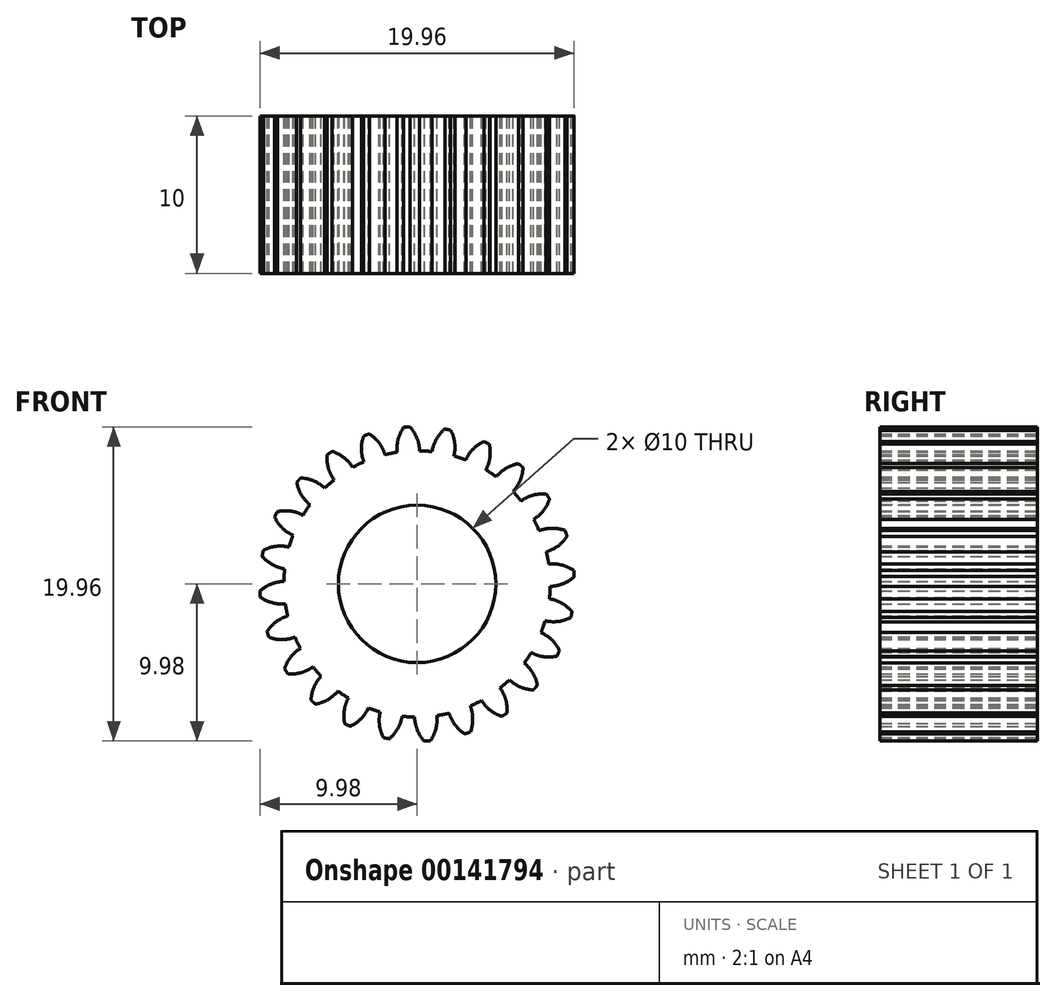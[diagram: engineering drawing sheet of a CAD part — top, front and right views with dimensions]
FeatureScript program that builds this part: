
annotation { "Feature Type Name" : "Feature", "Feature Type Description" : "" }
export const myFeature = defineFeature(function(context is Context, id is Id, definition is map)
    precondition{}
    {
        {
            var Q0;
            Q0=qCreatedBy(makeId("Front.planeOp"),FACE);
            var sketch = newSketch(context, id + "F0", { "sketchPlane" : qUnion([Q0])});
            skCircle(sketch, "E0", {"center": v(0, 0) * mm, "radius": 10 * mm, "construction": true});
            skCircle(sketch, "E1", {"center": v(0, 0) * mm, "radius": 8.46 * mm});
            skCircle(sketch, "E2", {"center": v(0, 0) * mm, "radius": 9.24 * mm, "construction": true});
            skLineSegment(sketch, "E3", {"start": v(0, 0) * mm, "end": v(0, 13.37) * mm, "construction": true});
            skLineSegment(sketch, "E4", {"start": v(0, 0) * mm, "end": v(-0.84, 12.82) * mm, "construction": true});
            skCircle(sketch, "E5", {"center": v(0, 9.24) * mm, "radius": 2.3 * mm, "construction": true});
            skLineSegment(sketch, "E6", {"start": v(0, 9.24) * mm, "end": v(-7.1, 9.24) * mm, "construction": true});
            skLineSegment(sketch, "E7", {"start": v(0, 9.24) * mm, "end": v(-6.72, 6.8) * mm, "construction": true});
            skCircle(sketch, "E8", {"center": v(0, 0) * mm, "radius": 8.68 * mm, "construction": true});
            skArc(sketch, "E9", {"start": v(0, 9.24) * mm, "mid": v(-0.2, 9.63) * mm, "end": v(-0.46, 9.98) * mm});
            skArc(sketch, "E10", {"start": v(0.15, 8.46) * mm, "mid": v(0.11, 8.86) * mm, "end": v(0, 9.24) * mm});
            skArc(sketch, "E11.MirrorCS", {"start": v(-1.2, 9.16) * mm, "mid": v(-1.06, 9.58) * mm, "end": v(-0.85, 9.96) * mm});
            skArc(sketch, "E12.MirrorCS", {"start": v(-1.26, 8.37) * mm, "mid": v(-1.27, 8.77) * mm, "end": v(-1.2, 9.16) * mm});
            skArc(sketch, "E13", {"start": v(-0.46, 9.98) * mm, "mid": v(-0.65, 9.98) * mm, "end": v(-0.85, 9.96) * mm});
            skArc(sketch, "E14.1.0", {"start": v(-3.54, 8.54) * mm, "mid": v(-3.5, 8.97) * mm, "end": v(-3.4, 9.4) * mm});
            skArc(sketch, "E14.1.1", {"start": v(-2.4, 8.93) * mm, "mid": v(-2.68, 9.25) * mm, "end": v(-3.03, 9.52) * mm});
            skArc(sketch, "E14.1.2", {"start": v(-2.04, 8.21) * mm, "mid": v(-2.18, 8.58) * mm, "end": v(-2.4, 8.93) * mm});
            skArc(sketch, "E14.1.3", {"start": v(-3.38, 7.76) * mm, "mid": v(-3.5, 8.14) * mm, "end": v(-3.54, 8.54) * mm});
            skArc(sketch, "E14.1.4", {"start": v(-3.03, 9.52) * mm, "mid": v(-3.21, 9.47) * mm, "end": v(-3.4, 9.4) * mm});
            skArc(sketch, "E14.2.0", {"start": v(-5.62, 7.33) * mm, "mid": v(-5.7, 7.76) * mm, "end": v(-5.71, 8.2) * mm});
            skArc(sketch, "E14.2.1", {"start": v(-4.62, 8) * mm, "mid": v(-4.99, 8.24) * mm, "end": v(-5.39, 8.41) * mm});
            skArc(sketch, "E14.2.2", {"start": v(-4.1, 7.4) * mm, "mid": v(-4.33, 7.73) * mm, "end": v(-4.62, 8) * mm});
            skArc(sketch, "E14.2.3", {"start": v(-5.27, 6.62) * mm, "mid": v(-5.48, 6.96) * mm, "end": v(-5.62, 7.33) * mm});
            skArc(sketch, "E14.2.4", {"start": v(-5.39, 8.41) * mm, "mid": v(-5.55, 8.31) * mm, "end": v(-5.71, 8.2) * mm});
            skArc(sketch, "E14.3.0", {"start": v(-7.33, 5.62) * mm, "mid": v(-7.52, 6.02) * mm, "end": v(-7.64, 6.44) * mm});
            skArc(sketch, "E14.3.1", {"start": v(-6.53, 6.53) * mm, "mid": v(-6.95, 6.67) * mm, "end": v(-7.38, 6.73) * mm});
            skArc(sketch, "E14.3.2", {"start": v(-5.87, 6.1) * mm, "mid": v(-6.18, 6.34) * mm, "end": v(-6.53, 6.53) * mm});
            skArc(sketch, "E14.3.3", {"start": v(-6.8, 5.03) * mm, "mid": v(-7.1, 5.3) * mm, "end": v(-7.33, 5.62) * mm});
            skArc(sketch, "E14.3.4", {"start": v(-7.38, 6.73) * mm, "mid": v(-7.52, 6.6) * mm, "end": v(-7.64, 6.44) * mm});
            skArc(sketch, "E14.4.0", {"start": v(-8.54, 3.54) * mm, "mid": v(-8.82, 3.87) * mm, "end": v(-9.04, 4.25) * mm});
            skArc(sketch, "E14.4.1", {"start": v(-8, 4.62) * mm, "mid": v(-8.44, 4.65) * mm, "end": v(-8.87, 4.6) * mm});
            skArc(sketch, "E14.4.2", {"start": v(-7.25, 4.36) * mm, "mid": v(-7.61, 4.52) * mm, "end": v(-8, 4.62) * mm});
            skArc(sketch, "E14.4.3", {"start": v(-7.87, 3.1) * mm, "mid": v(-8.22, 3.29) * mm, "end": v(-8.54, 3.54) * mm});
            skArc(sketch, "E14.4.4", {"start": v(-8.87, 4.6) * mm, "mid": v(-8.97, 4.42) * mm, "end": v(-9.04, 4.25) * mm});
            skArc(sketch, "E14.5.0", {"start": v(-9.16, 1.2) * mm, "mid": v(-9.52, 1.45) * mm, "end": v(-9.84, 1.76) * mm});
            skArc(sketch, "E14.5.1", {"start": v(-8.93, 2.4) * mm, "mid": v(-9.35, 2.3) * mm, "end": v(-9.76, 2.14) * mm});
            skArc(sketch, "E14.5.2", {"start": v(-8.13, 2.34) * mm, "mid": v(-8.53, 2.4) * mm, "end": v(-8.93, 2.4) * mm});
            skArc(sketch, "E14.5.3", {"start": v(-8.4, 0.95) * mm, "mid": v(-8.8, 1.05) * mm, "end": v(-9.16, 1.2) * mm});
            skArc(sketch, "E14.5.4", {"start": v(-9.76, 2.14) * mm, "mid": v(-9.8, 1.95) * mm, "end": v(-9.84, 1.76) * mm});
            skArc(sketch, "E14.6.0", {"start": v(-9.16, -1.2) * mm, "mid": v(-9.58, -1.06) * mm, "end": v(-9.96, -0.85) * mm});
            skArc(sketch, "E14.6.1", {"start": v(-9.24, 0) * mm, "mid": v(-9.63, -0.2) * mm, "end": v(-9.98, -0.46) * mm});
            skArc(sketch, "E14.6.2", {"start": v(-8.46, 0.15) * mm, "mid": v(-8.86, 0.11) * mm, "end": v(-9.24, 0) * mm});
            skArc(sketch, "E14.6.3", {"start": v(-8.37, -1.26) * mm, "mid": v(-8.77, -1.27) * mm, "end": v(-9.16, -1.2) * mm});
            skArc(sketch, "E14.6.4", {"start": v(-9.98, -0.46) * mm, "mid": v(-9.98, -0.65) * mm, "end": v(-9.96, -0.85) * mm});
            skArc(sketch, "E14.7.0", {"start": v(-8.54, -3.54) * mm, "mid": v(-8.97, -3.5) * mm, "end": v(-9.4, -3.4) * mm});
            skArc(sketch, "E14.7.1", {"start": v(-8.93, -2.4) * mm, "mid": v(-9.25, -2.68) * mm, "end": v(-9.52, -3.03) * mm});
            skArc(sketch, "E14.7.2", {"start": v(-8.21, -2.04) * mm, "mid": v(-8.58, -2.18) * mm, "end": v(-8.93, -2.4) * mm});
            skArc(sketch, "E14.7.3", {"start": v(-7.76, -3.38) * mm, "mid": v(-8.14, -3.5) * mm, "end": v(-8.54, -3.54) * mm});
            skArc(sketch, "E14.7.4", {"start": v(-9.52, -3.03) * mm, "mid": v(-9.47, -3.21) * mm, "end": v(-9.4, -3.4) * mm});
            skArc(sketch, "E14.8.0", {"start": v(-7.33, -5.62) * mm, "mid": v(-7.76, -5.7) * mm, "end": v(-8.2, -5.71) * mm});
            skArc(sketch, "E14.8.1", {"start": v(-8, -4.62) * mm, "mid": v(-8.24, -4.99) * mm, "end": v(-8.41, -5.39) * mm});
            skArc(sketch, "E14.8.2", {"start": v(-7.4, -4.1) * mm, "mid": v(-7.73, -4.33) * mm, "end": v(-8, -4.62) * mm});
            skArc(sketch, "E14.8.3", {"start": v(-6.62, -5.27) * mm, "mid": v(-6.96, -5.48) * mm, "end": v(-7.33, -5.62) * mm});
            skArc(sketch, "E14.8.4", {"start": v(-8.41, -5.39) * mm, "mid": v(-8.31, -5.55) * mm, "end": v(-8.2, -5.71) * mm});
            skArc(sketch, "E14.9.0", {"start": v(-5.62, -7.33) * mm, "mid": v(-6.02, -7.52) * mm, "end": v(-6.44, -7.64) * mm});
            skArc(sketch, "E14.9.1", {"start": v(-6.53, -6.53) * mm, "mid": v(-6.67, -6.95) * mm, "end": v(-6.73, -7.38) * mm});
            skArc(sketch, "E14.9.2", {"start": v(-6.1, -5.87) * mm, "mid": v(-6.34, -6.18) * mm, "end": v(-6.53, -6.53) * mm});
            skArc(sketch, "E14.9.3", {"start": v(-5.03, -6.8) * mm, "mid": v(-5.3, -7.1) * mm, "end": v(-5.62, -7.33) * mm});
            skArc(sketch, "E14.9.4", {"start": v(-6.73, -7.38) * mm, "mid": v(-6.6, -7.52) * mm, "end": v(-6.44, -7.64) * mm});
            skArc(sketch, "E14.10.0", {"start": v(-3.54, -8.54) * mm, "mid": v(-3.87, -8.82) * mm, "end": v(-4.25, -9.04) * mm});
            skArc(sketch, "E14.10.1", {"start": v(-4.62, -8) * mm, "mid": v(-4.65, -8.44) * mm, "end": v(-4.6, -8.87) * mm});
            skArc(sketch, "E14.10.2", {"start": v(-4.36, -7.25) * mm, "mid": v(-4.52, -7.61) * mm, "end": v(-4.62, -8) * mm});
            skArc(sketch, "E14.10.3", {"start": v(-3.1, -7.87) * mm, "mid": v(-3.29, -8.22) * mm, "end": v(-3.54, -8.54) * mm});
            skArc(sketch, "E14.10.4", {"start": v(-4.6, -8.87) * mm, "mid": v(-4.42, -8.97) * mm, "end": v(-4.25, -9.04) * mm});
            skArc(sketch, "E14.11.0", {"start": v(-1.2, -9.16) * mm, "mid": v(-1.45, -9.52) * mm, "end": v(-1.76, -9.84) * mm});
            skArc(sketch, "E14.11.1", {"start": v(-2.4, -8.93) * mm, "mid": v(-2.3, -9.35) * mm, "end": v(-2.14, -9.76) * mm});
            skArc(sketch, "E14.11.2", {"start": v(-2.34, -8.13) * mm, "mid": v(-2.4, -8.53) * mm, "end": v(-2.4, -8.93) * mm});
            skArc(sketch, "E14.11.3", {"start": v(-0.95, -8.4) * mm, "mid": v(-1.05, -8.8) * mm, "end": v(-1.2, -9.16) * mm});
            skArc(sketch, "E14.11.4", {"start": v(-2.14, -9.76) * mm, "mid": v(-1.95, -9.8) * mm, "end": v(-1.76, -9.84) * mm});
            skArc(sketch, "E14.12.0", {"start": v(1.2, -9.16) * mm, "mid": v(1.06, -9.58) * mm, "end": v(0.85, -9.96) * mm});
            skArc(sketch, "E14.12.1", {"start": v(0, -9.24) * mm, "mid": v(0.2, -9.63) * mm, "end": v(0.46, -9.98) * mm});
            skArc(sketch, "E14.12.2", {"start": v(-0.15, -8.46) * mm, "mid": v(-0.11, -8.86) * mm, "end": v(0, -9.24) * mm});
            skArc(sketch, "E14.12.3", {"start": v(1.26, -8.37) * mm, "mid": v(1.27, -8.77) * mm, "end": v(1.2, -9.16) * mm});
            skArc(sketch, "E14.12.4", {"start": v(0.46, -9.98) * mm, "mid": v(0.65, -9.98) * mm, "end": v(0.85, -9.96) * mm});
            skArc(sketch, "E14.13.0", {"start": v(3.54, -8.54) * mm, "mid": v(3.5, -8.97) * mm, "end": v(3.4, -9.4) * mm});
            skArc(sketch, "E14.13.1", {"start": v(2.4, -8.93) * mm, "mid": v(2.68, -9.25) * mm, "end": v(3.03, -9.52) * mm});
            skArc(sketch, "E14.13.2", {"start": v(2.04, -8.21) * mm, "mid": v(2.18, -8.58) * mm, "end": v(2.4, -8.93) * mm});
            skArc(sketch, "E14.13.3", {"start": v(3.38, -7.76) * mm, "mid": v(3.5, -8.14) * mm, "end": v(3.54, -8.54) * mm});
            skArc(sketch, "E14.13.4", {"start": v(3.03, -9.52) * mm, "mid": v(3.21, -9.47) * mm, "end": v(3.4, -9.4) * mm});
            skArc(sketch, "E14.14.0", {"start": v(5.62, -7.33) * mm, "mid": v(5.7, -7.76) * mm, "end": v(5.71, -8.2) * mm});
            skArc(sketch, "E14.14.1", {"start": v(4.62, -8) * mm, "mid": v(4.99, -8.24) * mm, "end": v(5.39, -8.41) * mm});
            skArc(sketch, "E14.14.2", {"start": v(4.1, -7.4) * mm, "mid": v(4.33, -7.73) * mm, "end": v(4.62, -8) * mm});
            skArc(sketch, "E14.14.3", {"start": v(5.27, -6.62) * mm, "mid": v(5.48, -6.96) * mm, "end": v(5.62, -7.33) * mm});
            skArc(sketch, "E14.14.4", {"start": v(5.39, -8.41) * mm, "mid": v(5.55, -8.31) * mm, "end": v(5.71, -8.2) * mm});
            skArc(sketch, "E14.15.0", {"start": v(7.33, -5.62) * mm, "mid": v(7.52, -6.02) * mm, "end": v(7.64, -6.44) * mm});
            skArc(sketch, "E14.15.1", {"start": v(6.53, -6.53) * mm, "mid": v(6.95, -6.67) * mm, "end": v(7.38, -6.73) * mm});
            skArc(sketch, "E14.15.2", {"start": v(5.87, -6.1) * mm, "mid": v(6.18, -6.34) * mm, "end": v(6.53, -6.53) * mm});
            skArc(sketch, "E14.15.3", {"start": v(6.8, -5.03) * mm, "mid": v(7.1, -5.3) * mm, "end": v(7.33, -5.62) * mm});
            skArc(sketch, "E14.15.4", {"start": v(7.38, -6.73) * mm, "mid": v(7.52, -6.6) * mm, "end": v(7.64, -6.44) * mm});
            skArc(sketch, "E14.16.0", {"start": v(8.54, -3.54) * mm, "mid": v(8.82, -3.87) * mm, "end": v(9.04, -4.25) * mm});
            skArc(sketch, "E14.16.1", {"start": v(8, -4.62) * mm, "mid": v(8.44, -4.65) * mm, "end": v(8.87, -4.6) * mm});
            skArc(sketch, "E14.16.2", {"start": v(7.25, -4.36) * mm, "mid": v(7.61, -4.52) * mm, "end": v(8, -4.62) * mm});
            skArc(sketch, "E14.16.3", {"start": v(7.87, -3.1) * mm, "mid": v(8.22, -3.29) * mm, "end": v(8.54, -3.54) * mm});
            skArc(sketch, "E14.16.4", {"start": v(8.87, -4.6) * mm, "mid": v(8.97, -4.42) * mm, "end": v(9.04, -4.25) * mm});
            skArc(sketch, "E14.17.0", {"start": v(9.16, -1.2) * mm, "mid": v(9.52, -1.45) * mm, "end": v(9.84, -1.76) * mm});
            skArc(sketch, "E14.17.1", {"start": v(8.93, -2.4) * mm, "mid": v(9.35, -2.3) * mm, "end": v(9.76, -2.14) * mm});
            skArc(sketch, "E14.17.2", {"start": v(8.13, -2.34) * mm, "mid": v(8.53, -2.4) * mm, "end": v(8.93, -2.4) * mm});
            skArc(sketch, "E14.17.3", {"start": v(8.4, -0.95) * mm, "mid": v(8.8, -1.05) * mm, "end": v(9.16, -1.2) * mm});
            skArc(sketch, "E14.17.4", {"start": v(9.76, -2.14) * mm, "mid": v(9.8, -1.95) * mm, "end": v(9.84, -1.76) * mm});
            skArc(sketch, "E14.18.0", {"start": v(9.16, 1.2) * mm, "mid": v(9.58, 1.06) * mm, "end": v(9.96, 0.85) * mm});
            skArc(sketch, "E14.18.1", {"start": v(9.24, 0) * mm, "mid": v(9.63, 0.2) * mm, "end": v(9.98, 0.46) * mm});
            skArc(sketch, "E14.18.2", {"start": v(8.46, -0.15) * mm, "mid": v(8.86, -0.11) * mm, "end": v(9.24, 0) * mm});
            skArc(sketch, "E14.18.3", {"start": v(8.37, 1.26) * mm, "mid": v(8.77, 1.27) * mm, "end": v(9.16, 1.2) * mm});
            skArc(sketch, "E14.18.4", {"start": v(9.98, 0.46) * mm, "mid": v(9.98, 0.65) * mm, "end": v(9.96, 0.85) * mm});
            skArc(sketch, "E14.19.0", {"start": v(8.54, 3.54) * mm, "mid": v(8.97, 3.5) * mm, "end": v(9.4, 3.4) * mm});
            skArc(sketch, "E14.19.1", {"start": v(8.93, 2.4) * mm, "mid": v(9.25, 2.68) * mm, "end": v(9.52, 3.03) * mm});
            skArc(sketch, "E14.19.2", {"start": v(8.21, 2.04) * mm, "mid": v(8.58, 2.18) * mm, "end": v(8.93, 2.4) * mm});
            skArc(sketch, "E14.19.3", {"start": v(7.76, 3.38) * mm, "mid": v(8.14, 3.5) * mm, "end": v(8.54, 3.54) * mm});
            skArc(sketch, "E14.19.4", {"start": v(9.52, 3.03) * mm, "mid": v(9.47, 3.21) * mm, "end": v(9.4, 3.4) * mm});
            skArc(sketch, "E14.20.0", {"start": v(7.33, 5.62) * mm, "mid": v(7.76, 5.7) * mm, "end": v(8.2, 5.71) * mm});
            skArc(sketch, "E14.20.1", {"start": v(8, 4.62) * mm, "mid": v(8.24, 4.99) * mm, "end": v(8.41, 5.39) * mm});
            skArc(sketch, "E14.20.2", {"start": v(7.4, 4.1) * mm, "mid": v(7.73, 4.33) * mm, "end": v(8, 4.62) * mm});
            skArc(sketch, "E14.20.3", {"start": v(6.62, 5.27) * mm, "mid": v(6.96, 5.48) * mm, "end": v(7.33, 5.62) * mm});
            skArc(sketch, "E14.20.4", {"start": v(8.41, 5.39) * mm, "mid": v(8.31, 5.55) * mm, "end": v(8.2, 5.71) * mm});
            skArc(sketch, "E14.21.0", {"start": v(5.62, 7.33) * mm, "mid": v(6.02, 7.52) * mm, "end": v(6.44, 7.64) * mm});
            skArc(sketch, "E14.21.1", {"start": v(6.53, 6.53) * mm, "mid": v(6.67, 6.95) * mm, "end": v(6.73, 7.38) * mm});
            skArc(sketch, "E14.21.2", {"start": v(6.1, 5.87) * mm, "mid": v(6.34, 6.18) * mm, "end": v(6.53, 6.53) * mm});
            skArc(sketch, "E14.21.3", {"start": v(5.03, 6.8) * mm, "mid": v(5.3, 7.1) * mm, "end": v(5.62, 7.33) * mm});
            skArc(sketch, "E14.21.4", {"start": v(6.73, 7.38) * mm, "mid": v(6.6, 7.52) * mm, "end": v(6.44, 7.64) * mm});
            skArc(sketch, "E14.22.0", {"start": v(3.54, 8.54) * mm, "mid": v(3.87, 8.82) * mm, "end": v(4.25, 9.04) * mm});
            skArc(sketch, "E14.22.1", {"start": v(4.62, 8) * mm, "mid": v(4.65, 8.44) * mm, "end": v(4.6, 8.87) * mm});
            skArc(sketch, "E14.22.2", {"start": v(4.36, 7.25) * mm, "mid": v(4.52, 7.61) * mm, "end": v(4.62, 8) * mm});
            skArc(sketch, "E14.22.3", {"start": v(3.1, 7.87) * mm, "mid": v(3.29, 8.22) * mm, "end": v(3.54, 8.54) * mm});
            skArc(sketch, "E14.22.4", {"start": v(4.6, 8.87) * mm, "mid": v(4.42, 8.97) * mm, "end": v(4.25, 9.04) * mm});
            skArc(sketch, "E14.23.0", {"start": v(1.2, 9.16) * mm, "mid": v(1.45, 9.52) * mm, "end": v(1.76, 9.84) * mm});
            skArc(sketch, "E14.23.1", {"start": v(2.4, 8.93) * mm, "mid": v(2.3, 9.35) * mm, "end": v(2.14, 9.76) * mm});
            skArc(sketch, "E14.23.2", {"start": v(2.34, 8.13) * mm, "mid": v(2.4, 8.53) * mm, "end": v(2.4, 8.93) * mm});
            skArc(sketch, "E14.23.3", {"start": v(0.95, 8.4) * mm, "mid": v(1.05, 8.8) * mm, "end": v(1.2, 9.16) * mm});
            skArc(sketch, "E14.23.4", {"start": v(2.14, 9.76) * mm, "mid": v(1.95, 9.8) * mm, "end": v(1.76, 9.84) * mm});
            skSolve(sketch);
        }
        {
            var Q0;
            Q0 = qSketchRegion(id + "F0", true);
            extrude(context, id + "F1", {"entities" : qUnion([Q0]), "depth" : 10 * mm});
        }
        {
            var Q0;
            Q0=makeQuery(id+"F1.opExtrude","CAP_FACE",FACE,{"disambiguationData":[OSD([sQuery(id+"F0.wireOp",EDGE,"E1"),sQuery(id+"F0.wireOp",EDGE,"E9"),sQuery(id+"F0.wireOp",EDGE,"E10"),sQuery(id+"F0.wireOp",EDGE,"E11.MirrorCS"),sQuery(id+"F0.wireOp",EDGE,"E12.MirrorCS"),sQuery(id+"F0.wireOp",EDGE,"E13"),sQuery(id+"F0.wireOp",EDGE,"E14.1.0"),sQuery(id+"F0.wireOp",EDGE,"E14.1.1"),sQuery(id+"F0.wireOp",EDGE,"E14.1.2"),sQuery(id+"F0.wireOp",EDGE,"E14.1.3"),sQuery(id+"F0.wireOp",EDGE,"E14.1.4"),sQuery(id+"F0.wireOp",EDGE,"E14.2.0"),sQuery(id+"F0.wireOp",EDGE,"E14.2.1"),sQuery(id+"F0.wireOp",EDGE,"E14.2.2"),sQuery(id+"F0.wireOp",EDGE,"E14.2.3"),sQuery(id+"F0.wireOp",EDGE,"E14.2.4"),sQuery(id+"F0.wireOp",EDGE,"E14.3.0"),sQuery(id+"F0.wireOp",EDGE,"E14.3.1"),sQuery(id+"F0.wireOp",EDGE,"E14.3.2"),sQuery(id+"F0.wireOp",EDGE,"E14.3.3"),sQuery(id+"F0.wireOp",EDGE,"E14.3.4"),sQuery(id+"F0.wireOp",EDGE,"E14.4.0"),sQuery(id+"F0.wireOp",EDGE,"E14.4.1"),sQuery(id+"F0.wireOp",EDGE,"E14.4.2"),sQuery(id+"F0.wireOp",EDGE,"E14.4.3"),sQuery(id+"F0.wireOp",EDGE,"E14.4.4"),sQuery(id+"F0.wireOp",EDGE,"E14.5.0"),sQuery(id+"F0.wireOp",EDGE,"E14.5.1"),sQuery(id+"F0.wireOp",EDGE,"E14.5.2"),sQuery(id+"F0.wireOp",EDGE,"E14.5.3"),sQuery(id+"F0.wireOp",EDGE,"E14.5.4"),sQuery(id+"F0.wireOp",EDGE,"E14.6.0"),sQuery(id+"F0.wireOp",EDGE,"E14.6.1"),sQuery(id+"F0.wireOp",EDGE,"E14.6.2"),sQuery(id+"F0.wireOp",EDGE,"E14.6.3"),sQuery(id+"F0.wireOp",EDGE,"E14.6.4"),sQuery(id+"F0.wireOp",EDGE,"E14.7.0"),sQuery(id+"F0.wireOp",EDGE,"E14.7.1"),sQuery(id+"F0.wireOp",EDGE,"E14.7.2"),sQuery(id+"F0.wireOp",EDGE,"E14.7.3"),sQuery(id+"F0.wireOp",EDGE,"E14.7.4"),sQuery(id+"F0.wireOp",EDGE,"E14.8.0"),sQuery(id+"F0.wireOp",EDGE,"E14.8.1"),sQuery(id+"F0.wireOp",EDGE,"E14.8.2"),sQuery(id+"F0.wireOp",EDGE,"E14.8.3"),sQuery(id+"F0.wireOp",EDGE,"E14.8.4"),sQuery(id+"F0.wireOp",EDGE,"E14.9.0"),sQuery(id+"F0.wireOp",EDGE,"E14.9.1"),sQuery(id+"F0.wireOp",EDGE,"E14.9.2"),sQuery(id+"F0.wireOp",EDGE,"E14.9.3"),sQuery(id+"F0.wireOp",EDGE,"E14.9.4"),sQuery(id+"F0.wireOp",EDGE,"E14.10.0"),sQuery(id+"F0.wireOp",EDGE,"E14.10.1"),sQuery(id+"F0.wireOp",EDGE,"E14.10.2"),sQuery(id+"F0.wireOp",EDGE,"E14.10.3"),sQuery(id+"F0.wireOp",EDGE,"E14.10.4"),sQuery(id+"F0.wireOp",EDGE,"E14.11.0"),sQuery(id+"F0.wireOp",EDGE,"E14.11.1"),sQuery(id+"F0.wireOp",EDGE,"E14.11.2"),sQuery(id+"F0.wireOp",EDGE,"E14.11.3"),sQuery(id+"F0.wireOp",EDGE,"E14.11.4"),sQuery(id+"F0.wireOp",EDGE,"E14.12.0"),sQuery(id+"F0.wireOp",EDGE,"E14.12.1"),sQuery(id+"F0.wireOp",EDGE,"E14.12.2"),sQuery(id+"F0.wireOp",EDGE,"E14.12.3"),sQuery(id+"F0.wireOp",EDGE,"E14.12.4"),sQuery(id+"F0.wireOp",EDGE,"E14.13.0"),sQuery(id+"F0.wireOp",EDGE,"E14.13.1"),sQuery(id+"F0.wireOp",EDGE,"E14.13.2"),sQuery(id+"F0.wireOp",EDGE,"E14.13.3"),sQuery(id+"F0.wireOp",EDGE,"E14.13.4"),sQuery(id+"F0.wireOp",EDGE,"E14.14.0"),sQuery(id+"F0.wireOp",EDGE,"E14.14.1"),sQuery(id+"F0.wireOp",EDGE,"E14.14.2"),sQuery(id+"F0.wireOp",EDGE,"E14.14.3"),sQuery(id+"F0.wireOp",EDGE,"E14.14.4"),sQuery(id+"F0.wireOp",EDGE,"E14.15.0"),sQuery(id+"F0.wireOp",EDGE,"E14.15.1"),sQuery(id+"F0.wireOp",EDGE,"E14.15.2"),sQuery(id+"F0.wireOp",EDGE,"E14.15.3"),sQuery(id+"F0.wireOp",EDGE,"E14.15.4"),sQuery(id+"F0.wireOp",EDGE,"E14.16.0"),sQuery(id+"F0.wireOp",EDGE,"E14.16.1"),sQuery(id+"F0.wireOp",EDGE,"E14.16.2"),sQuery(id+"F0.wireOp",EDGE,"E14.16.3"),sQuery(id+"F0.wireOp",EDGE,"E14.16.4"),sQuery(id+"F0.wireOp",EDGE,"E14.17.0"),sQuery(id+"F0.wireOp",EDGE,"E14.17.1"),sQuery(id+"F0.wireOp",EDGE,"E14.17.2"),sQuery(id+"F0.wireOp",EDGE,"E14.17.3"),sQuery(id+"F0.wireOp",EDGE,"E14.17.4"),sQuery(id+"F0.wireOp",EDGE,"E14.18.0"),sQuery(id+"F0.wireOp",EDGE,"E14.18.1"),sQuery(id+"F0.wireOp",EDGE,"E14.18.2"),sQuery(id+"F0.wireOp",EDGE,"E14.18.3"),sQuery(id+"F0.wireOp",EDGE,"E14.18.4"),sQuery(id+"F0.wireOp",EDGE,"E14.19.0"),sQuery(id+"F0.wireOp",EDGE,"E14.19.1"),sQuery(id+"F0.wireOp",EDGE,"E14.19.2"),sQuery(id+"F0.wireOp",EDGE,"E14.19.3"),sQuery(id+"F0.wireOp",EDGE,"E14.19.4"),sQuery(id+"F0.wireOp",EDGE,"E14.20.0"),sQuery(id+"F0.wireOp",EDGE,"E14.20.1"),sQuery(id+"F0.wireOp",EDGE,"E14.20.2"),sQuery(id+"F0.wireOp",EDGE,"E14.20.3"),sQuery(id+"F0.wireOp",EDGE,"E14.20.4"),sQuery(id+"F0.wireOp",EDGE,"E14.21.0"),sQuery(id+"F0.wireOp",EDGE,"E14.21.1"),sQuery(id+"F0.wireOp",EDGE,"E14.21.2"),sQuery(id+"F0.wireOp",EDGE,"E14.21.3"),sQuery(id+"F0.wireOp",EDGE,"E14.21.4"),sQuery(id+"F0.wireOp",EDGE,"E14.22.0"),sQuery(id+"F0.wireOp",EDGE,"E14.22.1"),sQuery(id+"F0.wireOp",EDGE,"E14.22.2"),sQuery(id+"F0.wireOp",EDGE,"E14.22.3"),sQuery(id+"F0.wireOp",EDGE,"E14.22.4"),sQuery(id+"F0.wireOp",EDGE,"E14.23.0"),sQuery(id+"F0.wireOp",EDGE,"E14.23.1"),sQuery(id+"F0.wireOp",EDGE,"E14.23.2"),sQuery(id+"F0.wireOp",EDGE,"E14.23.3"),sQuery(id+"F0.wireOp",EDGE,"E14.23.4")])],"isStart":false});
            var sketch = newSketch(context, id + "F2", { "sketchPlane" : qUnion([Q0])});
            skPoint(sketch, "E15", {"position": v(0, 0) * mm});
            skSolve(sketch);
        }
        {
            var Q0;
            Q0=makeQuery(id+"F1.opExtrude","SWEPT_BODY",BODY,{"disambiguationData":[OSD([sQuery(id+"F0.wireOp",EDGE,"E1"),sQuery(id+"F0.wireOp",EDGE,"E9"),sQuery(id+"F0.wireOp",EDGE,"E10"),sQuery(id+"F0.wireOp",EDGE,"E11.MirrorCS"),sQuery(id+"F0.wireOp",EDGE,"E12.MirrorCS"),sQuery(id+"F0.wireOp",EDGE,"E13"),sQuery(id+"F0.wireOp",EDGE,"E14.1.0"),sQuery(id+"F0.wireOp",EDGE,"E14.1.1"),sQuery(id+"F0.wireOp",EDGE,"E14.1.2"),sQuery(id+"F0.wireOp",EDGE,"E14.1.3"),sQuery(id+"F0.wireOp",EDGE,"E14.1.4"),sQuery(id+"F0.wireOp",EDGE,"E14.2.0"),sQuery(id+"F0.wireOp",EDGE,"E14.2.1"),sQuery(id+"F0.wireOp",EDGE,"E14.2.2"),sQuery(id+"F0.wireOp",EDGE,"E14.2.3"),sQuery(id+"F0.wireOp",EDGE,"E14.2.4"),sQuery(id+"F0.wireOp",EDGE,"E14.3.0"),sQuery(id+"F0.wireOp",EDGE,"E14.3.1"),sQuery(id+"F0.wireOp",EDGE,"E14.3.2"),sQuery(id+"F0.wireOp",EDGE,"E14.3.3"),sQuery(id+"F0.wireOp",EDGE,"E14.3.4"),sQuery(id+"F0.wireOp",EDGE,"E14.4.0"),sQuery(id+"F0.wireOp",EDGE,"E14.4.1"),sQuery(id+"F0.wireOp",EDGE,"E14.4.2"),sQuery(id+"F0.wireOp",EDGE,"E14.4.3"),sQuery(id+"F0.wireOp",EDGE,"E14.4.4"),sQuery(id+"F0.wireOp",EDGE,"E14.5.0"),sQuery(id+"F0.wireOp",EDGE,"E14.5.1"),sQuery(id+"F0.wireOp",EDGE,"E14.5.2"),sQuery(id+"F0.wireOp",EDGE,"E14.5.3"),sQuery(id+"F0.wireOp",EDGE,"E14.5.4"),sQuery(id+"F0.wireOp",EDGE,"E14.6.0"),sQuery(id+"F0.wireOp",EDGE,"E14.6.1"),sQuery(id+"F0.wireOp",EDGE,"E14.6.2"),sQuery(id+"F0.wireOp",EDGE,"E14.6.3"),sQuery(id+"F0.wireOp",EDGE,"E14.6.4"),sQuery(id+"F0.wireOp",EDGE,"E14.7.0"),sQuery(id+"F0.wireOp",EDGE,"E14.7.1"),sQuery(id+"F0.wireOp",EDGE,"E14.7.2"),sQuery(id+"F0.wireOp",EDGE,"E14.7.3"),sQuery(id+"F0.wireOp",EDGE,"E14.7.4"),sQuery(id+"F0.wireOp",EDGE,"E14.8.0"),sQuery(id+"F0.wireOp",EDGE,"E14.8.1"),sQuery(id+"F0.wireOp",EDGE,"E14.8.2"),sQuery(id+"F0.wireOp",EDGE,"E14.8.3"),sQuery(id+"F0.wireOp",EDGE,"E14.8.4"),sQuery(id+"F0.wireOp",EDGE,"E14.9.0"),sQuery(id+"F0.wireOp",EDGE,"E14.9.1"),sQuery(id+"F0.wireOp",EDGE,"E14.9.2"),sQuery(id+"F0.wireOp",EDGE,"E14.9.3"),sQuery(id+"F0.wireOp",EDGE,"E14.9.4"),sQuery(id+"F0.wireOp",EDGE,"E14.10.0"),sQuery(id+"F0.wireOp",EDGE,"E14.10.1"),sQuery(id+"F0.wireOp",EDGE,"E14.10.2"),sQuery(id+"F0.wireOp",EDGE,"E14.10.3"),sQuery(id+"F0.wireOp",EDGE,"E14.10.4"),sQuery(id+"F0.wireOp",EDGE,"E14.11.0"),sQuery(id+"F0.wireOp",EDGE,"E14.11.1"),sQuery(id+"F0.wireOp",EDGE,"E14.11.2"),sQuery(id+"F0.wireOp",EDGE,"E14.11.3"),sQuery(id+"F0.wireOp",EDGE,"E14.11.4"),sQuery(id+"F0.wireOp",EDGE,"E14.12.0"),sQuery(id+"F0.wireOp",EDGE,"E14.12.1"),sQuery(id+"F0.wireOp",EDGE,"E14.12.2"),sQuery(id+"F0.wireOp",EDGE,"E14.12.3"),sQuery(id+"F0.wireOp",EDGE,"E14.12.4"),sQuery(id+"F0.wireOp",EDGE,"E14.13.0"),sQuery(id+"F0.wireOp",EDGE,"E14.13.1"),sQuery(id+"F0.wireOp",EDGE,"E14.13.2"),sQuery(id+"F0.wireOp",EDGE,"E14.13.3"),sQuery(id+"F0.wireOp",EDGE,"E14.13.4"),sQuery(id+"F0.wireOp",EDGE,"E14.14.0"),sQuery(id+"F0.wireOp",EDGE,"E14.14.1"),sQuery(id+"F0.wireOp",EDGE,"E14.14.2"),sQuery(id+"F0.wireOp",EDGE,"E14.14.3"),sQuery(id+"F0.wireOp",EDGE,"E14.14.4"),sQuery(id+"F0.wireOp",EDGE,"E14.15.0"),sQuery(id+"F0.wireOp",EDGE,"E14.15.1"),sQuery(id+"F0.wireOp",EDGE,"E14.15.2"),sQuery(id+"F0.wireOp",EDGE,"E14.15.3"),sQuery(id+"F0.wireOp",EDGE,"E14.15.4"),sQuery(id+"F0.wireOp",EDGE,"E14.16.0"),sQuery(id+"F0.wireOp",EDGE,"E14.16.1"),sQuery(id+"F0.wireOp",EDGE,"E14.16.2"),sQuery(id+"F0.wireOp",EDGE,"E14.16.3"),sQuery(id+"F0.wireOp",EDGE,"E14.16.4"),sQuery(id+"F0.wireOp",EDGE,"E14.17.0"),sQuery(id+"F0.wireOp",EDGE,"E14.17.1"),sQuery(id+"F0.wireOp",EDGE,"E14.17.2"),sQuery(id+"F0.wireOp",EDGE,"E14.17.3"),sQuery(id+"F0.wireOp",EDGE,"E14.17.4"),sQuery(id+"F0.wireOp",EDGE,"E14.18.0"),sQuery(id+"F0.wireOp",EDGE,"E14.18.1"),sQuery(id+"F0.wireOp",EDGE,"E14.18.2"),sQuery(id+"F0.wireOp",EDGE,"E14.18.3"),sQuery(id+"F0.wireOp",EDGE,"E14.18.4"),sQuery(id+"F0.wireOp",EDGE,"E14.19.0"),sQuery(id+"F0.wireOp",EDGE,"E14.19.1"),sQuery(id+"F0.wireOp",EDGE,"E14.19.2"),sQuery(id+"F0.wireOp",EDGE,"E14.19.3"),sQuery(id+"F0.wireOp",EDGE,"E14.19.4"),sQuery(id+"F0.wireOp",EDGE,"E14.20.0"),sQuery(id+"F0.wireOp",EDGE,"E14.20.1"),sQuery(id+"F0.wireOp",EDGE,"E14.20.2"),sQuery(id+"F0.wireOp",EDGE,"E14.20.3"),sQuery(id+"F0.wireOp",EDGE,"E14.20.4"),sQuery(id+"F0.wireOp",EDGE,"E14.21.0"),sQuery(id+"F0.wireOp",EDGE,"E14.21.1"),sQuery(id+"F0.wireOp",EDGE,"E14.21.2"),sQuery(id+"F0.wireOp",EDGE,"E14.21.3"),sQuery(id+"F0.wireOp",EDGE,"E14.21.4"),sQuery(id+"F0.wireOp",EDGE,"E14.22.0"),sQuery(id+"F0.wireOp",EDGE,"E14.22.1"),sQuery(id+"F0.wireOp",EDGE,"E14.22.2"),sQuery(id+"F0.wireOp",EDGE,"E14.22.3"),sQuery(id+"F0.wireOp",EDGE,"E14.22.4"),sQuery(id+"F0.wireOp",EDGE,"E14.23.0"),sQuery(id+"F0.wireOp",EDGE,"E14.23.1"),sQuery(id+"F0.wireOp",EDGE,"E14.23.2"),sQuery(id+"F0.wireOp",EDGE,"E14.23.3"),sQuery(id+"F0.wireOp",EDGE,"E14.23.4")])]});
            transform(context, id + "F3", {"entities" : qUnion([Q0]), "transformType" : TransformType.TRANSLATION_3D, "dx" : 0 * mm, "dy" : 0 * mm, "dz" : 0 * mm, "makeCopy" : true});
        }
        {
            var Q0;
            Q0=sQuery(id+"F2.wireOp",VERTEX,"E15");
            var Q1;
            Q1=makeQuery(id+"F1.opExtrude","SWEPT_BODY",BODY,{"disambiguationData":[OSD([sQuery(id+"F0.wireOp",EDGE,"E1"),sQuery(id+"F0.wireOp",EDGE,"E9"),sQuery(id+"F0.wireOp",EDGE,"E10"),sQuery(id+"F0.wireOp",EDGE,"E11.MirrorCS"),sQuery(id+"F0.wireOp",EDGE,"E12.MirrorCS"),sQuery(id+"F0.wireOp",EDGE,"E13"),sQuery(id+"F0.wireOp",EDGE,"E14.1.0"),sQuery(id+"F0.wireOp",EDGE,"E14.1.1"),sQuery(id+"F0.wireOp",EDGE,"E14.1.2"),sQuery(id+"F0.wireOp",EDGE,"E14.1.3"),sQuery(id+"F0.wireOp",EDGE,"E14.1.4"),sQuery(id+"F0.wireOp",EDGE,"E14.2.0"),sQuery(id+"F0.wireOp",EDGE,"E14.2.1"),sQuery(id+"F0.wireOp",EDGE,"E14.2.2"),sQuery(id+"F0.wireOp",EDGE,"E14.2.3"),sQuery(id+"F0.wireOp",EDGE,"E14.2.4"),sQuery(id+"F0.wireOp",EDGE,"E14.3.0"),sQuery(id+"F0.wireOp",EDGE,"E14.3.1"),sQuery(id+"F0.wireOp",EDGE,"E14.3.2"),sQuery(id+"F0.wireOp",EDGE,"E14.3.3"),sQuery(id+"F0.wireOp",EDGE,"E14.3.4"),sQuery(id+"F0.wireOp",EDGE,"E14.4.0"),sQuery(id+"F0.wireOp",EDGE,"E14.4.1"),sQuery(id+"F0.wireOp",EDGE,"E14.4.2"),sQuery(id+"F0.wireOp",EDGE,"E14.4.3"),sQuery(id+"F0.wireOp",EDGE,"E14.4.4"),sQuery(id+"F0.wireOp",EDGE,"E14.5.0"),sQuery(id+"F0.wireOp",EDGE,"E14.5.1"),sQuery(id+"F0.wireOp",EDGE,"E14.5.2"),sQuery(id+"F0.wireOp",EDGE,"E14.5.3"),sQuery(id+"F0.wireOp",EDGE,"E14.5.4"),sQuery(id+"F0.wireOp",EDGE,"E14.6.0"),sQuery(id+"F0.wireOp",EDGE,"E14.6.1"),sQuery(id+"F0.wireOp",EDGE,"E14.6.2"),sQuery(id+"F0.wireOp",EDGE,"E14.6.3"),sQuery(id+"F0.wireOp",EDGE,"E14.6.4"),sQuery(id+"F0.wireOp",EDGE,"E14.7.0"),sQuery(id+"F0.wireOp",EDGE,"E14.7.1"),sQuery(id+"F0.wireOp",EDGE,"E14.7.2"),sQuery(id+"F0.wireOp",EDGE,"E14.7.3"),sQuery(id+"F0.wireOp",EDGE,"E14.7.4"),sQuery(id+"F0.wireOp",EDGE,"E14.8.0"),sQuery(id+"F0.wireOp",EDGE,"E14.8.1"),sQuery(id+"F0.wireOp",EDGE,"E14.8.2"),sQuery(id+"F0.wireOp",EDGE,"E14.8.3"),sQuery(id+"F0.wireOp",EDGE,"E14.8.4"),sQuery(id+"F0.wireOp",EDGE,"E14.9.0"),sQuery(id+"F0.wireOp",EDGE,"E14.9.1"),sQuery(id+"F0.wireOp",EDGE,"E14.9.2"),sQuery(id+"F0.wireOp",EDGE,"E14.9.3"),sQuery(id+"F0.wireOp",EDGE,"E14.9.4"),sQuery(id+"F0.wireOp",EDGE,"E14.10.0"),sQuery(id+"F0.wireOp",EDGE,"E14.10.1"),sQuery(id+"F0.wireOp",EDGE,"E14.10.2"),sQuery(id+"F0.wireOp",EDGE,"E14.10.3"),sQuery(id+"F0.wireOp",EDGE,"E14.10.4"),sQuery(id+"F0.wireOp",EDGE,"E14.11.0"),sQuery(id+"F0.wireOp",EDGE,"E14.11.1"),sQuery(id+"F0.wireOp",EDGE,"E14.11.2"),sQuery(id+"F0.wireOp",EDGE,"E14.11.3"),sQuery(id+"F0.wireOp",EDGE,"E14.11.4"),sQuery(id+"F0.wireOp",EDGE,"E14.12.0"),sQuery(id+"F0.wireOp",EDGE,"E14.12.1"),sQuery(id+"F0.wireOp",EDGE,"E14.12.2"),sQuery(id+"F0.wireOp",EDGE,"E14.12.3"),sQuery(id+"F0.wireOp",EDGE,"E14.12.4"),sQuery(id+"F0.wireOp",EDGE,"E14.13.0"),sQuery(id+"F0.wireOp",EDGE,"E14.13.1"),sQuery(id+"F0.wireOp",EDGE,"E14.13.2"),sQuery(id+"F0.wireOp",EDGE,"E14.13.3"),sQuery(id+"F0.wireOp",EDGE,"E14.13.4"),sQuery(id+"F0.wireOp",EDGE,"E14.14.0"),sQuery(id+"F0.wireOp",EDGE,"E14.14.1"),sQuery(id+"F0.wireOp",EDGE,"E14.14.2"),sQuery(id+"F0.wireOp",EDGE,"E14.14.3"),sQuery(id+"F0.wireOp",EDGE,"E14.14.4"),sQuery(id+"F0.wireOp",EDGE,"E14.15.0"),sQuery(id+"F0.wireOp",EDGE,"E14.15.1"),sQuery(id+"F0.wireOp",EDGE,"E14.15.2"),sQuery(id+"F0.wireOp",EDGE,"E14.15.3"),sQuery(id+"F0.wireOp",EDGE,"E14.15.4"),sQuery(id+"F0.wireOp",EDGE,"E14.16.0"),sQuery(id+"F0.wireOp",EDGE,"E14.16.1"),sQuery(id+"F0.wireOp",EDGE,"E14.16.2"),sQuery(id+"F0.wireOp",EDGE,"E14.16.3"),sQuery(id+"F0.wireOp",EDGE,"E14.16.4"),sQuery(id+"F0.wireOp",EDGE,"E14.17.0"),sQuery(id+"F0.wireOp",EDGE,"E14.17.1"),sQuery(id+"F0.wireOp",EDGE,"E14.17.2"),sQuery(id+"F0.wireOp",EDGE,"E14.17.3"),sQuery(id+"F0.wireOp",EDGE,"E14.17.4"),sQuery(id+"F0.wireOp",EDGE,"E14.18.0"),sQuery(id+"F0.wireOp",EDGE,"E14.18.1"),sQuery(id+"F0.wireOp",EDGE,"E14.18.2"),sQuery(id+"F0.wireOp",EDGE,"E14.18.3"),sQuery(id+"F0.wireOp",EDGE,"E14.18.4"),sQuery(id+"F0.wireOp",EDGE,"E14.19.0"),sQuery(id+"F0.wireOp",EDGE,"E14.19.1"),sQuery(id+"F0.wireOp",EDGE,"E14.19.2"),sQuery(id+"F0.wireOp",EDGE,"E14.19.3"),sQuery(id+"F0.wireOp",EDGE,"E14.19.4"),sQuery(id+"F0.wireOp",EDGE,"E14.20.0"),sQuery(id+"F0.wireOp",EDGE,"E14.20.1"),sQuery(id+"F0.wireOp",EDGE,"E14.20.2"),sQuery(id+"F0.wireOp",EDGE,"E14.20.3"),sQuery(id+"F0.wireOp",EDGE,"E14.20.4"),sQuery(id+"F0.wireOp",EDGE,"E14.21.0"),sQuery(id+"F0.wireOp",EDGE,"E14.21.1"),sQuery(id+"F0.wireOp",EDGE,"E14.21.2"),sQuery(id+"F0.wireOp",EDGE,"E14.21.3"),sQuery(id+"F0.wireOp",EDGE,"E14.21.4"),sQuery(id+"F0.wireOp",EDGE,"E14.22.0"),sQuery(id+"F0.wireOp",EDGE,"E14.22.1"),sQuery(id+"F0.wireOp",EDGE,"E14.22.2"),sQuery(id+"F0.wireOp",EDGE,"E14.22.3"),sQuery(id+"F0.wireOp",EDGE,"E14.22.4"),sQuery(id+"F0.wireOp",EDGE,"E14.23.0"),sQuery(id+"F0.wireOp",EDGE,"E14.23.1"),sQuery(id+"F0.wireOp",EDGE,"E14.23.2"),sQuery(id+"F0.wireOp",EDGE,"E14.23.3"),sQuery(id+"F0.wireOp",EDGE,"E14.23.4")])]});
            hole(context, id + "F4", {"style" : HoleStyle.SIMPLE, "endStyle" : HoleEndStyle.BLIND, "holeDiameter" : 2 * mm, "holeDepth" : 5 * mm, "startFromSketch" : true, "locations" : qUnion([Q0]), "scope" : qUnion([Q1])});
        }
        {
            var Q0;
            Q0=makeQuery(id+"F3.opPattern","COPY",FACE,{"derivedFrom":makeQuery(id+"F1.opExtrude","CAP_FACE",FACE,{"disambiguationData":[OSD([sQuery(id+"F0.wireOp",EDGE,"E1"),sQuery(id+"F0.wireOp",EDGE,"E9"),sQuery(id+"F0.wireOp",EDGE,"E10"),sQuery(id+"F0.wireOp",EDGE,"E11.MirrorCS"),sQuery(id+"F0.wireOp",EDGE,"E12.MirrorCS"),sQuery(id+"F0.wireOp",EDGE,"E13"),sQuery(id+"F0.wireOp",EDGE,"E14.1.0"),sQuery(id+"F0.wireOp",EDGE,"E14.1.1"),sQuery(id+"F0.wireOp",EDGE,"E14.1.2"),sQuery(id+"F0.wireOp",EDGE,"E14.1.3"),sQuery(id+"F0.wireOp",EDGE,"E14.1.4"),sQuery(id+"F0.wireOp",EDGE,"E14.2.0"),sQuery(id+"F0.wireOp",EDGE,"E14.2.1"),sQuery(id+"F0.wireOp",EDGE,"E14.2.2"),sQuery(id+"F0.wireOp",EDGE,"E14.2.3"),sQuery(id+"F0.wireOp",EDGE,"E14.2.4"),sQuery(id+"F0.wireOp",EDGE,"E14.3.0"),sQuery(id+"F0.wireOp",EDGE,"E14.3.1"),sQuery(id+"F0.wireOp",EDGE,"E14.3.2"),sQuery(id+"F0.wireOp",EDGE,"E14.3.3"),sQuery(id+"F0.wireOp",EDGE,"E14.3.4"),sQuery(id+"F0.wireOp",EDGE,"E14.4.0"),sQuery(id+"F0.wireOp",EDGE,"E14.4.1"),sQuery(id+"F0.wireOp",EDGE,"E14.4.2"),sQuery(id+"F0.wireOp",EDGE,"E14.4.3"),sQuery(id+"F0.wireOp",EDGE,"E14.4.4"),sQuery(id+"F0.wireOp",EDGE,"E14.5.0"),sQuery(id+"F0.wireOp",EDGE,"E14.5.1"),sQuery(id+"F0.wireOp",EDGE,"E14.5.2"),sQuery(id+"F0.wireOp",EDGE,"E14.5.3"),sQuery(id+"F0.wireOp",EDGE,"E14.5.4"),sQuery(id+"F0.wireOp",EDGE,"E14.6.0"),sQuery(id+"F0.wireOp",EDGE,"E14.6.1"),sQuery(id+"F0.wireOp",EDGE,"E14.6.2"),sQuery(id+"F0.wireOp",EDGE,"E14.6.3"),sQuery(id+"F0.wireOp",EDGE,"E14.6.4"),sQuery(id+"F0.wireOp",EDGE,"E14.7.0"),sQuery(id+"F0.wireOp",EDGE,"E14.7.1"),sQuery(id+"F0.wireOp",EDGE,"E14.7.2"),sQuery(id+"F0.wireOp",EDGE,"E14.7.3"),sQuery(id+"F0.wireOp",EDGE,"E14.7.4"),sQuery(id+"F0.wireOp",EDGE,"E14.8.0"),sQuery(id+"F0.wireOp",EDGE,"E14.8.1"),sQuery(id+"F0.wireOp",EDGE,"E14.8.2"),sQuery(id+"F0.wireOp",EDGE,"E14.8.3"),sQuery(id+"F0.wireOp",EDGE,"E14.8.4"),sQuery(id+"F0.wireOp",EDGE,"E14.9.0"),sQuery(id+"F0.wireOp",EDGE,"E14.9.1"),sQuery(id+"F0.wireOp",EDGE,"E14.9.2"),sQuery(id+"F0.wireOp",EDGE,"E14.9.3"),sQuery(id+"F0.wireOp",EDGE,"E14.9.4"),sQuery(id+"F0.wireOp",EDGE,"E14.10.0"),sQuery(id+"F0.wireOp",EDGE,"E14.10.1"),sQuery(id+"F0.wireOp",EDGE,"E14.10.2"),sQuery(id+"F0.wireOp",EDGE,"E14.10.3"),sQuery(id+"F0.wireOp",EDGE,"E14.10.4"),sQuery(id+"F0.wireOp",EDGE,"E14.11.0"),sQuery(id+"F0.wireOp",EDGE,"E14.11.1"),sQuery(id+"F0.wireOp",EDGE,"E14.11.2"),sQuery(id+"F0.wireOp",EDGE,"E14.11.3"),sQuery(id+"F0.wireOp",EDGE,"E14.11.4"),sQuery(id+"F0.wireOp",EDGE,"E14.12.0"),sQuery(id+"F0.wireOp",EDGE,"E14.12.1"),sQuery(id+"F0.wireOp",EDGE,"E14.12.2"),sQuery(id+"F0.wireOp",EDGE,"E14.12.3"),sQuery(id+"F0.wireOp",EDGE,"E14.12.4"),sQuery(id+"F0.wireOp",EDGE,"E14.13.0"),sQuery(id+"F0.wireOp",EDGE,"E14.13.1"),sQuery(id+"F0.wireOp",EDGE,"E14.13.2"),sQuery(id+"F0.wireOp",EDGE,"E14.13.3"),sQuery(id+"F0.wireOp",EDGE,"E14.13.4"),sQuery(id+"F0.wireOp",EDGE,"E14.14.0"),sQuery(id+"F0.wireOp",EDGE,"E14.14.1"),sQuery(id+"F0.wireOp",EDGE,"E14.14.2"),sQuery(id+"F0.wireOp",EDGE,"E14.14.3"),sQuery(id+"F0.wireOp",EDGE,"E14.14.4"),sQuery(id+"F0.wireOp",EDGE,"E14.15.0"),sQuery(id+"F0.wireOp",EDGE,"E14.15.1"),sQuery(id+"F0.wireOp",EDGE,"E14.15.2"),sQuery(id+"F0.wireOp",EDGE,"E14.15.3"),sQuery(id+"F0.wireOp",EDGE,"E14.15.4"),sQuery(id+"F0.wireOp",EDGE,"E14.16.0"),sQuery(id+"F0.wireOp",EDGE,"E14.16.1"),sQuery(id+"F0.wireOp",EDGE,"E14.16.2"),sQuery(id+"F0.wireOp",EDGE,"E14.16.3"),sQuery(id+"F0.wireOp",EDGE,"E14.16.4"),sQuery(id+"F0.wireOp",EDGE,"E14.17.0"),sQuery(id+"F0.wireOp",EDGE,"E14.17.1"),sQuery(id+"F0.wireOp",EDGE,"E14.17.2"),sQuery(id+"F0.wireOp",EDGE,"E14.17.3"),sQuery(id+"F0.wireOp",EDGE,"E14.17.4"),sQuery(id+"F0.wireOp",EDGE,"E14.18.0"),sQuery(id+"F0.wireOp",EDGE,"E14.18.1"),sQuery(id+"F0.wireOp",EDGE,"E14.18.2"),sQuery(id+"F0.wireOp",EDGE,"E14.18.3"),sQuery(id+"F0.wireOp",EDGE,"E14.18.4"),sQuery(id+"F0.wireOp",EDGE,"E14.19.0"),sQuery(id+"F0.wireOp",EDGE,"E14.19.1"),sQuery(id+"F0.wireOp",EDGE,"E14.19.2"),sQuery(id+"F0.wireOp",EDGE,"E14.19.3"),sQuery(id+"F0.wireOp",EDGE,"E14.19.4"),sQuery(id+"F0.wireOp",EDGE,"E14.20.0"),sQuery(id+"F0.wireOp",EDGE,"E14.20.1"),sQuery(id+"F0.wireOp",EDGE,"E14.20.2"),sQuery(id+"F0.wireOp",EDGE,"E14.20.3"),sQuery(id+"F0.wireOp",EDGE,"E14.20.4"),sQuery(id+"F0.wireOp",EDGE,"E14.21.0"),sQuery(id+"F0.wireOp",EDGE,"E14.21.1"),sQuery(id+"F0.wireOp",EDGE,"E14.21.2"),sQuery(id+"F0.wireOp",EDGE,"E14.21.3"),sQuery(id+"F0.wireOp",EDGE,"E14.21.4"),sQuery(id+"F0.wireOp",EDGE,"E14.22.0"),sQuery(id+"F0.wireOp",EDGE,"E14.22.1"),sQuery(id+"F0.wireOp",EDGE,"E14.22.2"),sQuery(id+"F0.wireOp",EDGE,"E14.22.3"),sQuery(id+"F0.wireOp",EDGE,"E14.22.4"),sQuery(id+"F0.wireOp",EDGE,"E14.23.0"),sQuery(id+"F0.wireOp",EDGE,"E14.23.1"),sQuery(id+"F0.wireOp",EDGE,"E14.23.2"),sQuery(id+"F0.wireOp",EDGE,"E14.23.3"),sQuery(id+"F0.wireOp",EDGE,"E14.23.4")])],"isStart":false}),"instanceName":"1"});
            var sketch = newSketch(context, id + "F5", { "sketchPlane" : qUnion([Q0])});
            skCircle(sketch, "E16", {"center": v(0, 0) * mm, "radius": 5 * mm});
            skSolve(sketch);
        }
        {
            var Q0;
            Q0 = qSketchRegion(id + "F5", true);
            extrude(context, id + "F6", {"entities" : qUnion([Q0]), "operationType" : NewBodyOperationType.REMOVE, "oppositeDirection" : true, "depth" : 25 * mm});
        }
    });
